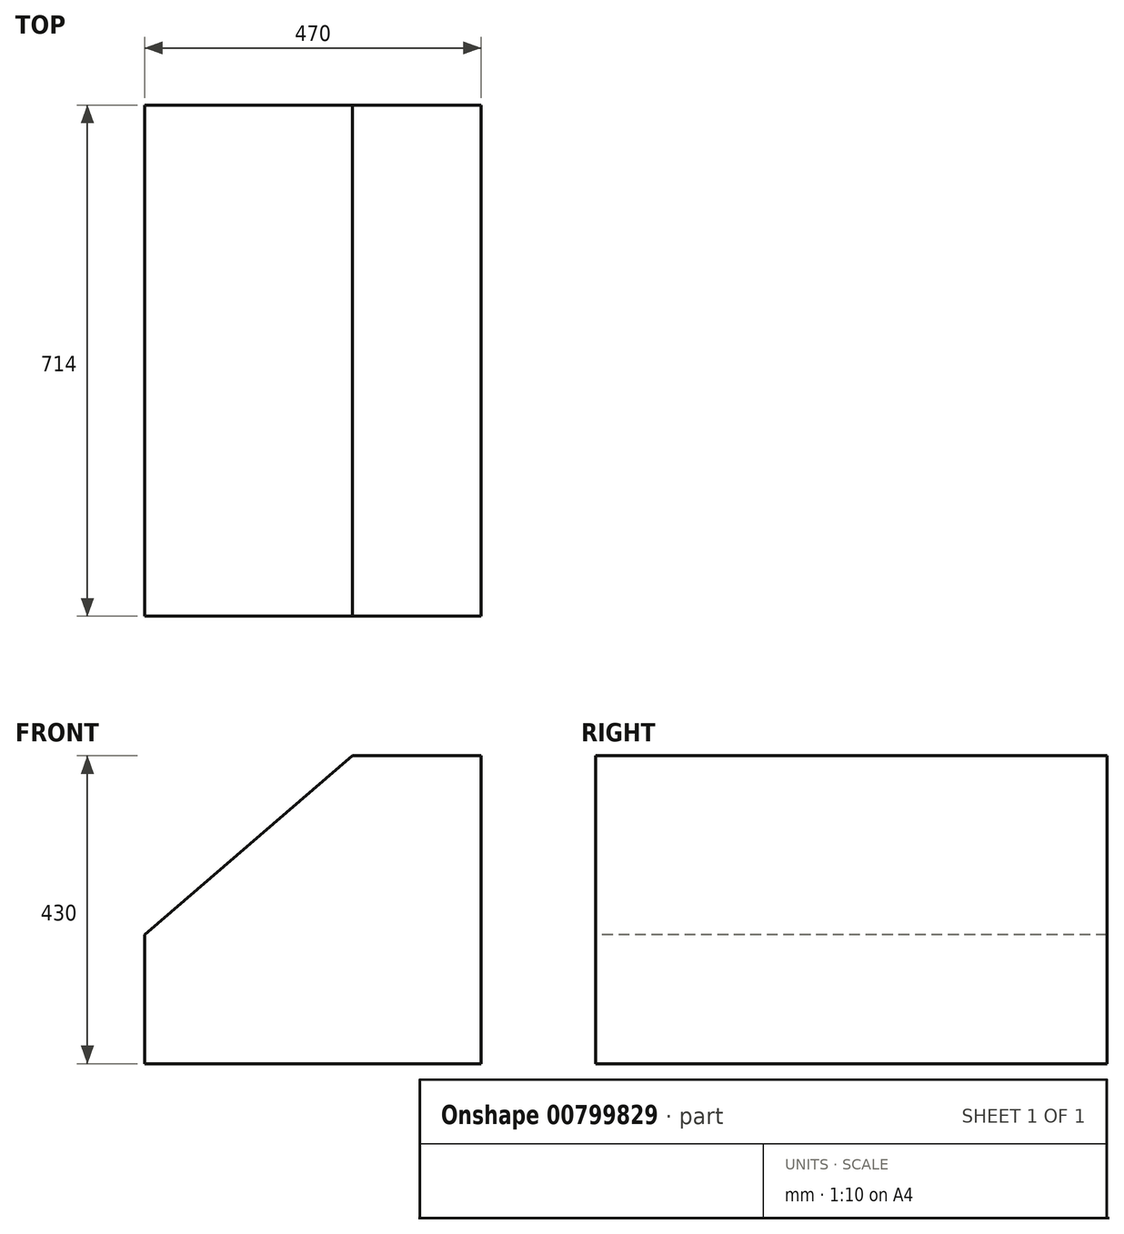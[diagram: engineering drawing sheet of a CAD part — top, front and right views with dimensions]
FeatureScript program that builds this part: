
annotation { "Feature Type Name" : "Feature", "Feature Type Description" : "" }
export const myFeature = defineFeature(function(context is Context, id is Id, definition is map)
    precondition{}
    {
        {
            var Q0;
            Q0=qCreatedBy(makeId("Front.planeOp"),FACE);
            var sketch = newSketch(context, id + "F0", { "sketchPlane" : qUnion([Q0])});
            skLineSegment(sketch, "E0", {"start": v(-96.5, -102.69) * mm, "end": v(373.5, -102.69) * mm});
            skLineSegment(sketch, "E1", {"start": v(373.5, -102.69) * mm, "end": v(373.5, 327.31) * mm});
            skLineSegment(sketch, "E2", {"start": v(373.5, 327.31) * mm, "end": v(193.5, 327.31) * mm});
            skLineSegment(sketch, "E3", {"start": v(-96.5, -102.69) * mm, "end": v(-96.5, 77.31) * mm});
            skLineSegment(sketch, "E4", {"start": v(-96.5, 77.31) * mm, "end": v(193.5, 327.31) * mm});
            skSolve(sketch);
        }
        {
            var Q0;
            Q0=sQuery(id+"F0.wireOp",EDGE,"E4");
            var Q1;
            Q1=sQuery(id+"F0.wireOp",EDGE,"E2");
            var Q2;
            Q2=sQuery(id+"F0.wireOp",EDGE,"E1");
            var Q3;
            Q3=sQuery(id+"F0.wireOp",EDGE,"E0");
            var Q4;
            Q4=sQuery(id+"F0.wireOp",EDGE,"E3");
            extrude(context, id + "F1", {"bodyType" : ToolBodyType.SURFACE, "surfaceEntities" : qUnion([Q0, Q1, Q2, Q3, Q4]), "depth" : 714 * mm, "offsetDistance" : 25 * mm});
        }
    });
